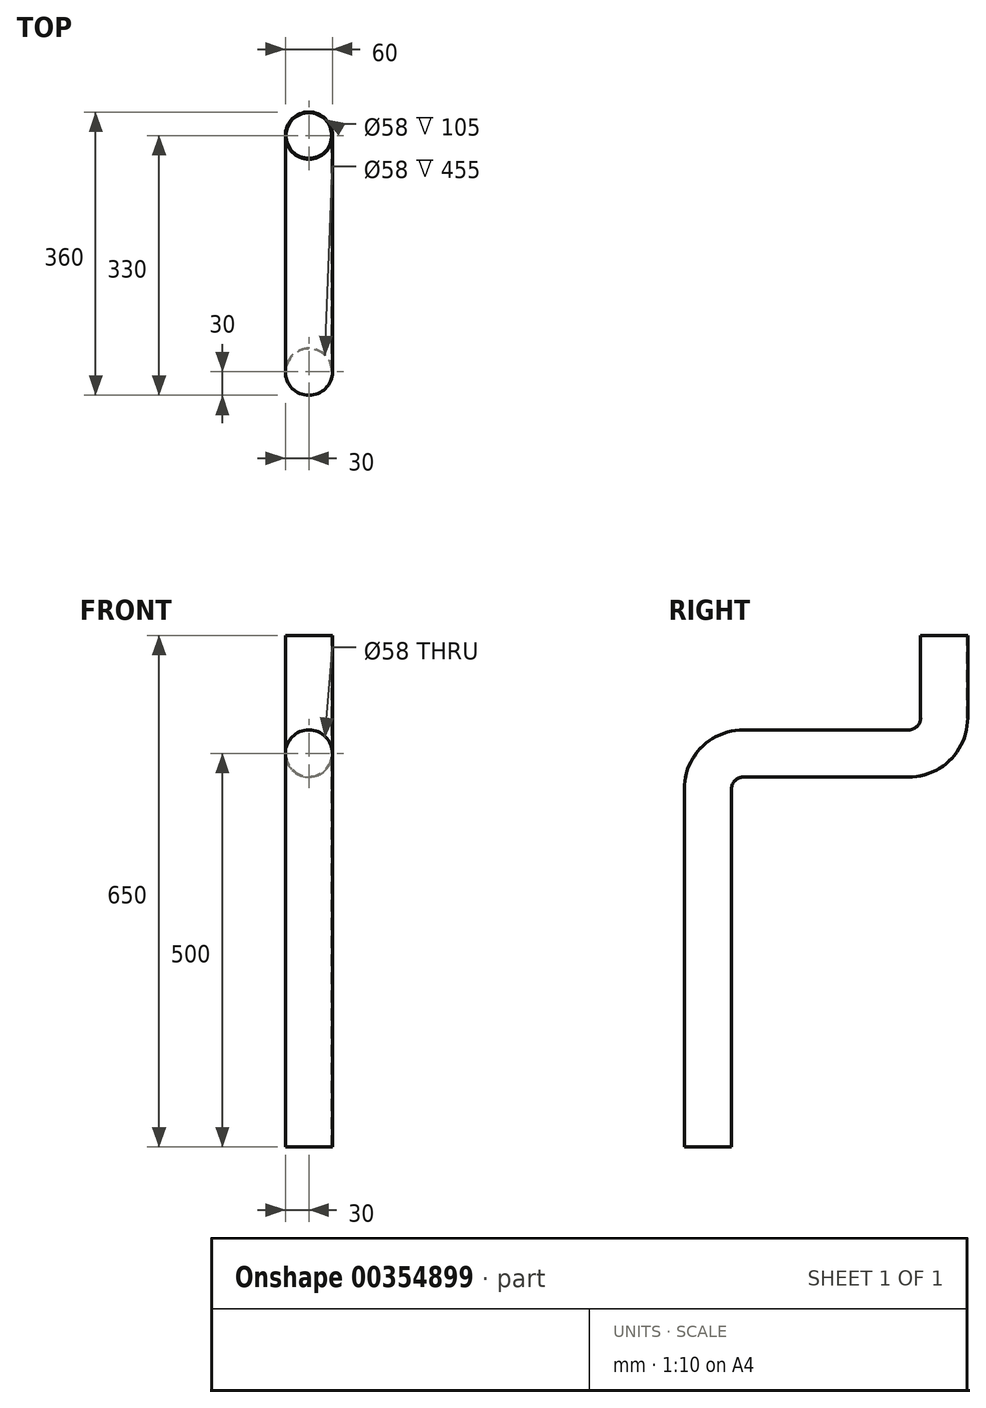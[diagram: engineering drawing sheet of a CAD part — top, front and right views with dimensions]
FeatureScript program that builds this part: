
annotation { "Feature Type Name" : "Feature", "Feature Type Description" : "" }
export const myFeature = defineFeature(function(context is Context, id is Id, definition is map)
    precondition{}
    {
        {
            var Q0;
            Q0=qCreatedBy(makeId("Right.planeOp"),FACE);
            var sketch = newSketch(context, id + "F0", { "sketchPlane" : qUnion([Q0])});
            skLineSegment(sketch, "E0", {"start": v(0, 0) * mm, "end": v(0, 455) * mm});
            skLineSegment(sketch, "E1", {"start": v(45, 500) * mm, "end": v(255, 500) * mm});
            skLineSegment(sketch, "E2", {"start": v(300, 545) * mm, "end": v(300, 650) * mm});
            skPoint(sketch, "E3.visualSharp", {"position": v(300, 500) * mm});
            skArc(sketch, "E3.filletArc", {"start": v(255, 500) * mm, "mid": v(286.82, 513.18) * mm, "end": v(300, 545) * mm});
            skPoint(sketch, "E4.visualSharp", {"position": v(0, 500) * mm});
            skArc(sketch, "E4.filletArc", {"start": v(45, 500) * mm, "mid": v(13.18, 486.82) * mm, "end": v(0, 455) * mm});
            skSolve(sketch);
        }
        {
            var Q0;
            Q0=qCreatedBy(makeId("Top.planeOp"),FACE);
            var sketch = newSketch(context, id + "F1", { "sketchPlane" : qUnion([Q0])});
            skCircle(sketch, "E5", {"center": v(0, 0) * mm, "radius": 30 * mm});
            skCircle(sketch, "E6", {"center": v(0, 0) * mm, "radius": 29 * mm});
            skSolve(sketch);
        }
        {
            var Q0;
            Q0=makeQuery(id+"F1.imprint","IMPRINT",FACE,{"disambiguationData":[TD([[makeQuery(id+"F1.imprint","IMPRINT",EDGE,{"derivedFrom":sQuery(id+"F1.wireOp",EDGE,"E5")}),1.0]])]});
            var Q1;
            Q1=sQuery(id+"F0.wireOp",EDGE,"E0");
            var Q2;
            Q2=sQuery(id+"F0.wireOp",EDGE,"E4.filletArc");
            var Q3;
            Q3=sQuery(id+"F0.wireOp",EDGE,"E1");
            var Q4;
            Q4=sQuery(id+"F0.wireOp",EDGE,"E3.filletArc");
            var Q5;
            Q5=sQuery(id+"F0.wireOp",EDGE,"E2");
            sweep(context, id + "F2", {"profiles" : qUnion([Q0]), "path" : qUnion([Q1, Q2, Q3, Q4, Q5])});
        }
    });
